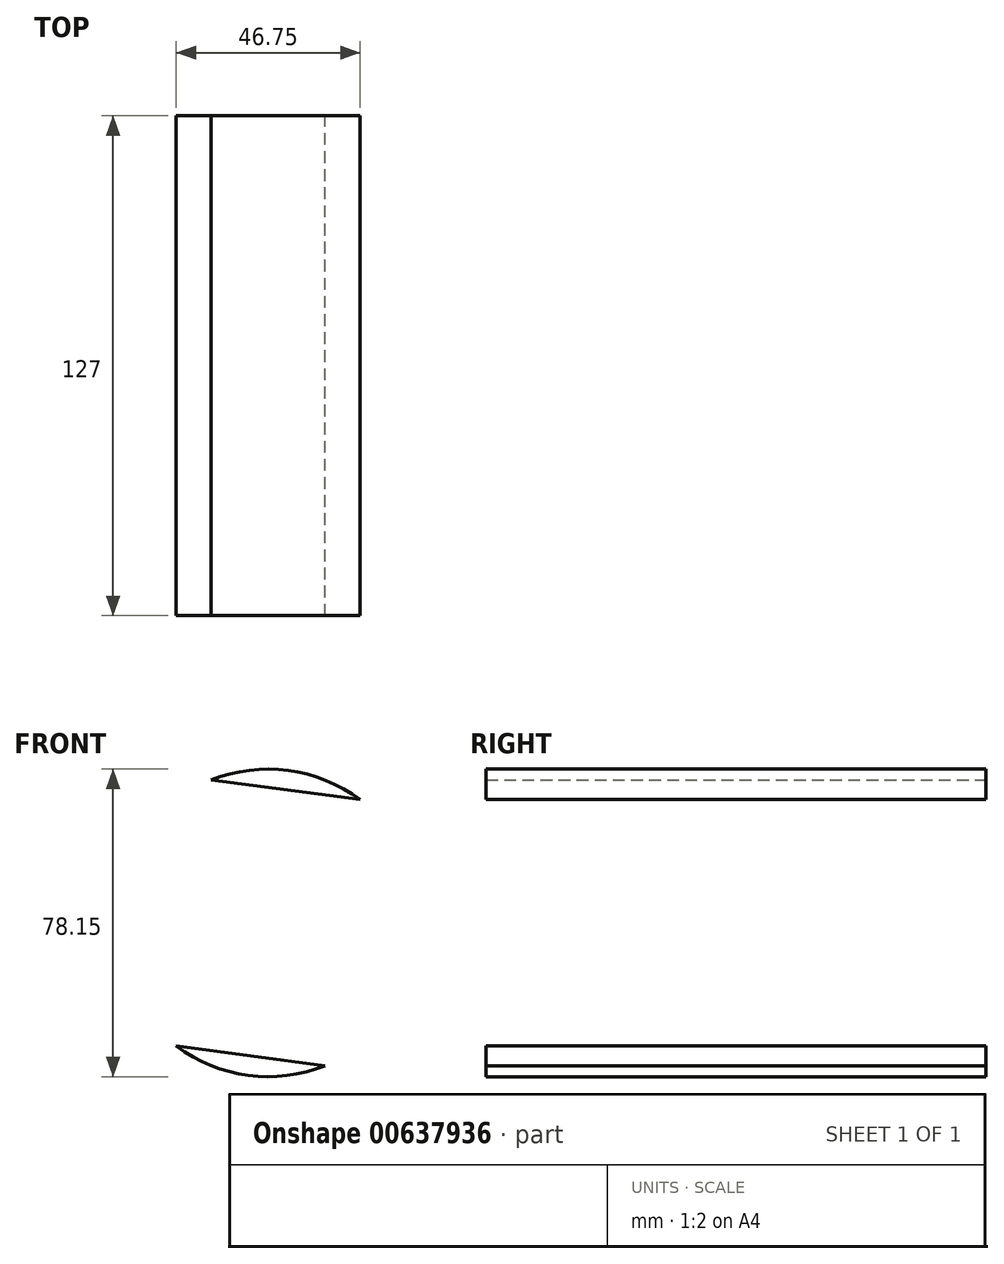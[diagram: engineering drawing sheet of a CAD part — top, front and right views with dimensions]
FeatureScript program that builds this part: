
annotation { "Feature Type Name" : "Feature", "Feature Type Description" : "" }
export const myFeature = defineFeature(function(context is Context, id is Id, definition is map)
    precondition{}
    {
        {
            var Q0;
            Q0=qCreatedBy(makeId("Front.planeOp"),FACE);
            var sketch = newSketch(context, id + "F0", { "sketchPlane" : qUnion([Q0])});
            skArc(sketch, "E0", {"start": v(51.39, 56.06) * mm, "mid": v(-10.73, 29.84) * mm, "end": v(42.51, -11.53) * mm});
            skLineSegment(sketch, "E1", {"start": v(42.51, -11.53) * mm, "end": v(51.39, 56.06) * mm});
            skSolve(sketch);
        }
        {
            var Q0;
            Q0=makeQuery(id+"F0.imprint","IMPRINT",FACE,{"disambiguationData":[TD([[makeQuery(id+"F0.imprint","IMPRINT",EDGE,{"derivedFrom":sQuery(id+"F0.wireOp",EDGE,"E0")}),1.0]])]});
            extrude(context, id + "F1", {"entities" : qUnion([Q0]), "depth" : 127 * mm, "offsetDistance" : 25.4 * mm});
        }
        {
            var Q0;
            Q0=makeQuery(id+"F1.opExtrude","SWEPT_FACE",FACE,{"disambiguationData":[OSD([sQuery(id+"F0.wireOp",EDGE,"E1")])]});
            var sketch = newSketch(context, id + "F2", { "sketchPlane" : qUnion([Q0])});
            skArc(sketch, "E2", {"start": v(-78.43, 15.24) * mm, "mid": v(-47.7, 44.74) * mm, "end": v(-87.34, 29.12) * mm});
            skArc(sketch, "E3", {"start": v(-78.43, 15.24) * mm, "mid": v(-81.6, 23) * mm, "end": v(-87.34, 29.12) * mm});
            skSolve(sketch);
        }
        {
            var Q0;
            Q0 = qSketchRegion(id + "F2", true);
            var Q1;
            {var subQ2=sQuery(id+"F2.wireOp",EDGE,"E3");Q1=makeQuery(id+"F2.imprint","IMPRINT",FACE,{"disambiguationData":[TD([[makeQuery(id+"F2.imprint","IMPRINT",EDGE,{"derivedFrom":subQ2}),1.0]])]});}
            var Q2;
            {var subQ0=sQuery(id+"F2.wireOp",EDGE,"E3");Q2=makeQuery(id+"F2.imprint","IMPRINT",FACE,{"disambiguationData":[TD([[makeQuery(id+"F2.imprint","IMPRINT",EDGE,{"derivedFrom":subQ0}),-1.0]])]});}
            extrude(context, id + "F3", {"entities" : qUnion([Q0, Q1, Q2]), "operationType" : NewBodyOperationType.REMOVE, "endBound" : BoundingType.UP_TO_NEXT, "oppositeDirection" : true, "depth" : 50.8 * mm, "offsetDistance" : 25.4 * mm});
        }
    });
